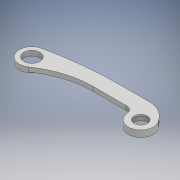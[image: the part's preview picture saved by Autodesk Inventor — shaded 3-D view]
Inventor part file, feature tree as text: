
AUTODESK INVENTOR PART (.ipt)
format: ipt  version: 2017 (Build 210142000, 142)  size: 307,712 bytes
history: native  units: mm
features: extrude x4, sketch x4, fillet x1, projected_geometry x1
ambient origin geometry x8: Origin, YZ Plane, XZ Plane, XY Plane, X Axis, Y Axis, Z Axis, Center Point
bodies: Solid1 (feature_tree)
feature tree (10):
  extrude  "Extrusion1"  Depth=22.0mm
  extrude  "Extrusion2"  Depth=74.2mm
  fillet  "Fillet1"  Radius=6.0mm
  extrude  "Extrusion3"  Depth=6.0mm TaperAngle=0.0deg
  extrude  "Extrusion5"  Depth=3.0mm
  sketch  "Sketch1"  dims[d0=22.0mm d1=22.0mm]
  sketch  "Sketch2"  dims[d2=148.4mm d3=74.2mm d4=6.0mm]
  sketch  "Sketch3"  dims[d5=6.0mm d6=6.0mm d7=0.0mm]
  sketch  "Sketch5"  dims[d8=9.0mm d9=0.0mm d10=3.0mm d12=20.0mm d13=2.0mm d14=0.0mm d30=2.0mm d31=0.0mm d32=18.0mm]
  projected_geometry  "Projected Loop1"
